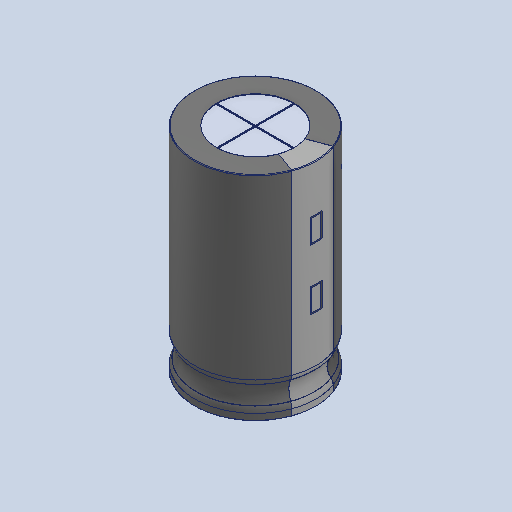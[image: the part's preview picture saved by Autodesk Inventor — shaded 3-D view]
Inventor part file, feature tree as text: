
AUTODESK INVENTOR PART (.ipt)
format: ipt  version: 2023.1 (Build 271208000, 208)  size: 527,360 bytes
history: native  units: in
note: dims shown in document units (in); Inventor stores cm internally (conversion verified against a paired STEP export)
features: other x4, fillet x2
ambient origin geometry x8: Origin, YZ Plane, XZ Plane, XY Plane, X Axis, Y Axis, Z Axis, Center Point
bodies: Solid1 (feature_tree), Solid2 (feature_tree), Solid3 (feature_tree), Solid4 (feature_tree), Solid5 (feature_tree), Solid6 (feature_tree)
feature tree (6):
  other  "CROSS 2"
  other  "LEADS HOLES"
  other  "LEADS[2]"
  other  "2ND LEAD EXTENDED"
  fillet  "Fillet6"  [1 undecoded]
  fillet  "Fillet5"  [1 undecoded]
note: 2 required parameter values undecoded (feature->parameter linkage not recoverable at this tier; creation-order binding heuristic only, values carry confidence <= 0.55)
